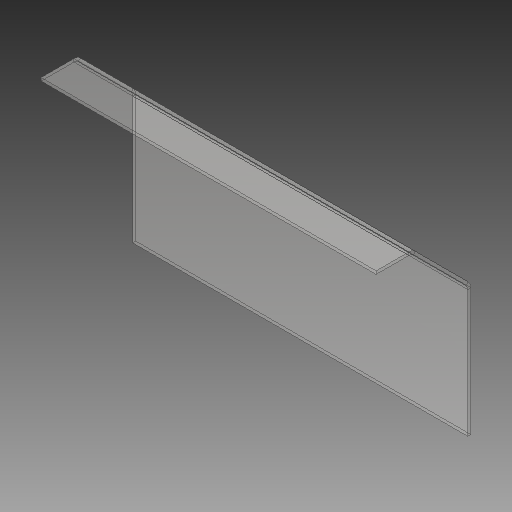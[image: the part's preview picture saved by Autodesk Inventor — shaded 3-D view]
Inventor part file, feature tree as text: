
AUTODESK INVENTOR PART (.ipt)
format: ipt  version: 2018 (Build 220112000, 112)  size: 164,352 bytes
history: native  units: mm
features: sheet_metal_op x7, sketch x3, other x3
ambient origin geometry x8: Origin, YZ Plane, XZ Plane, XY Plane, X Axis, Y Axis, Z Axis, Center Point
bodies: Solid1 (feature_tree)
feature tree (13):
  sheet_metal_op  "Face1"
  sheet_metal_op  "Flange1"
  sheet_metal_op  "Flange2"
  sketch  "Sketch1"  dims[d0=1100.0mm]
  other  "Plate1"
  sketch  "Sketch2"  dims[d1=430.0mm]
  other  "Plate2"
  sheet_metal_op  "Bend1"
  sheet_metal_op  "Corner1"
  sketch  "Sketch3"  dims[d2=10.0mm d3=10.0mm d4=5.0mm d5=20.0mm d6=10.0mm d7=270.0mm d8=45.0deg d9=20.0mm d10=40.0mm d11=10.0mm d12=10.0mm d13=10.0mm d14=5.0mm d15=20.0mm d16=10.0mm d17=120.0mm d18=45.0deg d19=20.0mm d20=40.0mm d21=10.0mm d22=10.0mm]
  other  "Plate3"
  sheet_metal_op  "Bend2"
  sheet_metal_op  "Corner2"
